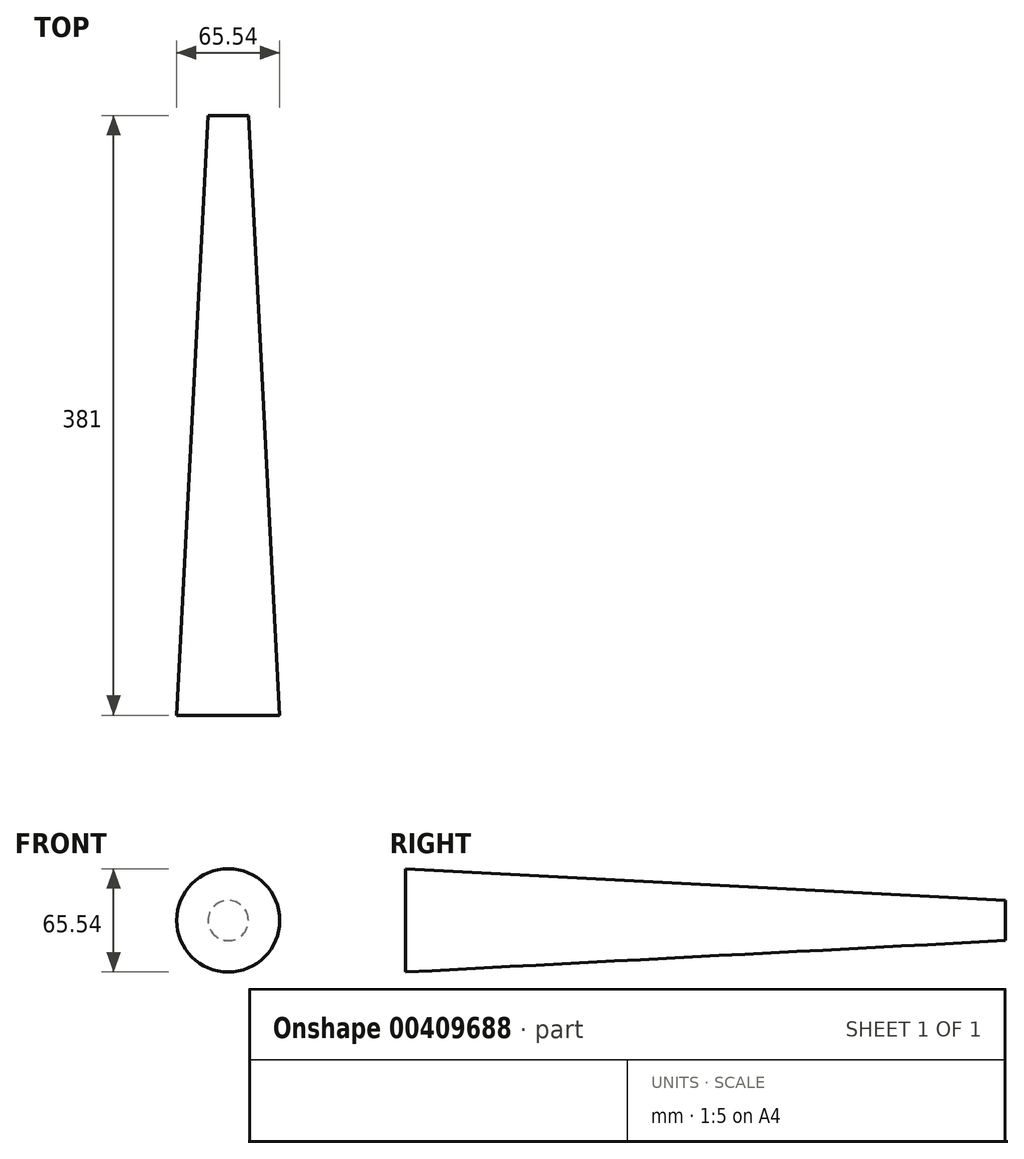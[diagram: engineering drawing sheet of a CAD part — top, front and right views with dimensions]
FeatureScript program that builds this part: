
annotation { "Feature Type Name" : "Feature", "Feature Type Description" : "" }
export const myFeature = defineFeature(function(context is Context, id is Id, definition is map)
    precondition{}
    {
        {
            var Q0;
            Q0=qCreatedBy(makeId("Front.planeOp"),FACE);
            var sketch = newSketch(context, id + "F0", { "sketchPlane" : qUnion([Q0])});
            skCircle(sketch, "E0", {"center": v(0, 0) * mm, "radius": 12.8 * mm});
            skSolve(sketch);
        }
        {
            var Q0;
            Q0 = qSketchRegion(id + "F0", true);
            extrude(context, id + "F1", {"entities" : qUnion([Q0]), "depth" : 381 * mm, "hasDraft" : true, "draftAngle" : 3 * degree});
        }
    });
